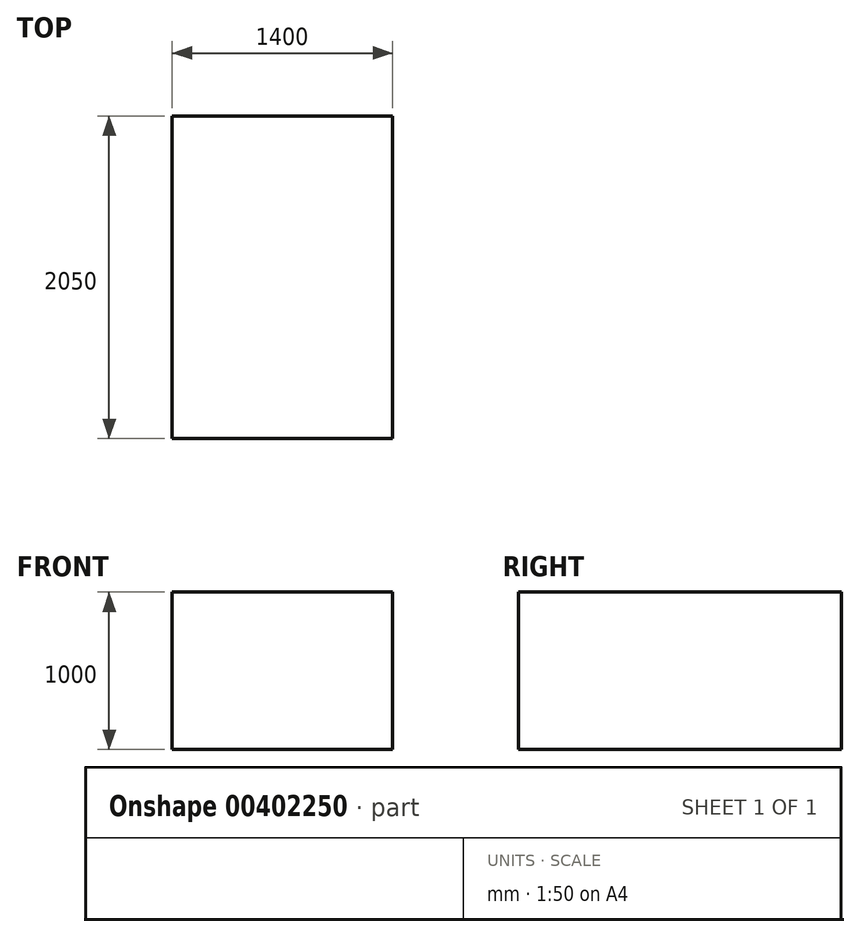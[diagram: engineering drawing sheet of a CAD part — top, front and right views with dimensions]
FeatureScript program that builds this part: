
annotation { "Feature Type Name" : "Feature", "Feature Type Description" : "" }
export const myFeature = defineFeature(function(context is Context, id is Id, definition is map)
    precondition{}
    {
        {
            var Q0;
            Q0=qCreatedBy(makeId("Top.planeOp"),FACE);
            var sketch = newSketch(context, id + "F0", { "sketchPlane" : qUnion([Q0])});
            skLineSegment(sketch, "E0.bottom", {"start": v(0, 0) * mm, "end": v(1400, 0) * mm});
            skLineSegment(sketch, "E0.top", {"start": v(0, 2050) * mm, "end": v(1400, 2050) * mm});
            skLineSegment(sketch, "E0.left", {"start": v(0, 0) * mm, "end": v(0, 2050) * mm});
            skLineSegment(sketch, "E0.right", {"start": v(1400, 0) * mm, "end": v(1400, 2050) * mm});
            skSolve(sketch);
        }
        {
            var Q0;
            Q0 = qSketchRegion(id + "F0", true);
            extrude(context, id + "F1", {"entities" : qUnion([Q0]), "depth" : 1000 * mm});
        }
    });
